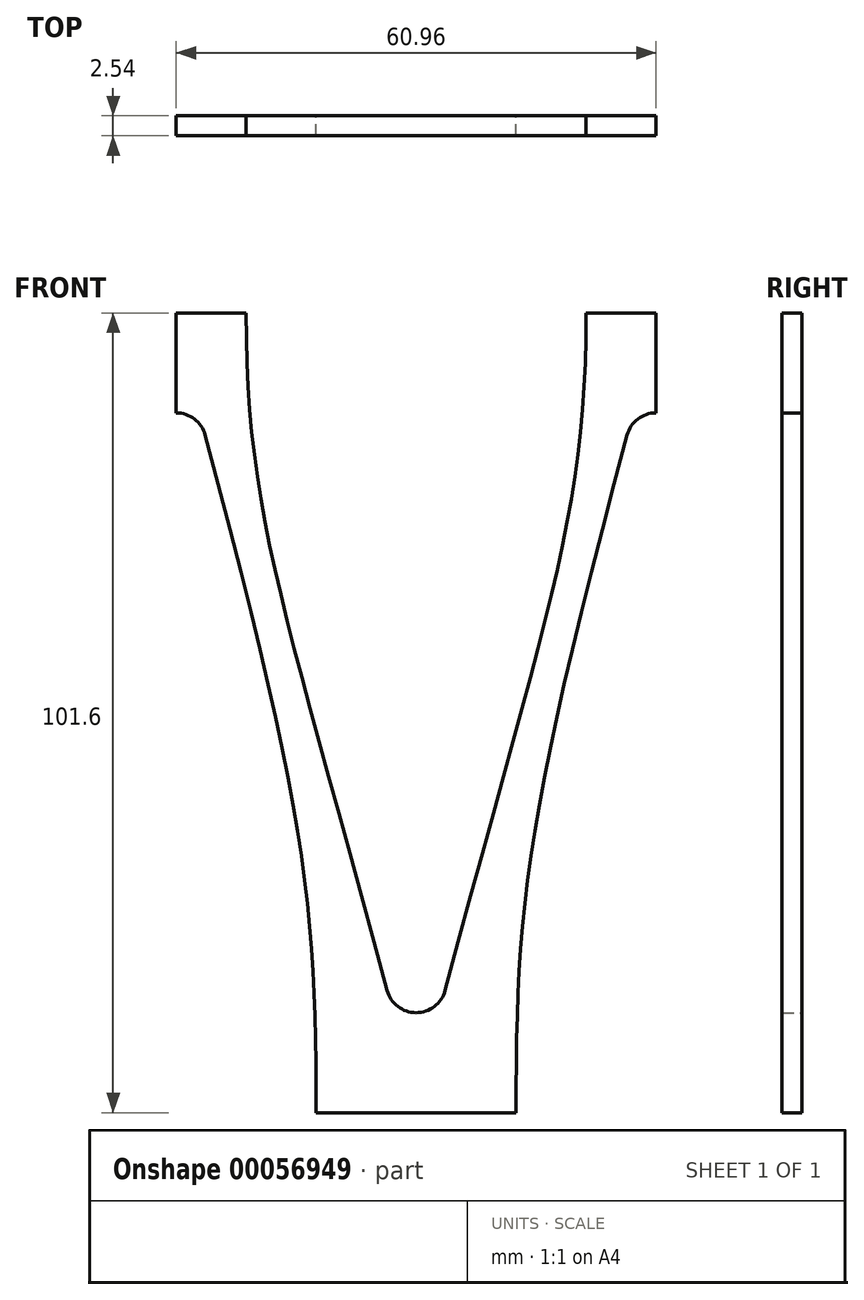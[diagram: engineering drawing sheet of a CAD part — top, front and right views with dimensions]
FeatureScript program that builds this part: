
annotation { "Feature Type Name" : "Feature", "Feature Type Description" : "" }
export const myFeature = defineFeature(function(context is Context, id is Id, definition is map)
    precondition{}
    {
        {
            var Q0;
            Q0=qCreatedBy(makeId("Front.planeOp"),FACE);
            var sketch = newSketch(context, id + "F0", { "sketchPlane" : qUnion([Q0])});
            skLineSegment(sketch, "E0", {"start": v(38.1, 139.7) * mm, "end": v(46.99, 139.7) * mm});
            skLineSegment(sketch, "E1", {"start": v(55.88, 38.1) * mm, "end": v(68.58, 38.1) * mm});
            skLineSegment(sketch, "E2", {"start": v(68.58, 38.1) * mm, "end": v(68.58, 50.8) * mm});
            skLineSegment(sketch, "E3", {"start": v(38.1, 139.7) * mm, "end": v(38.1, 127) * mm});
            skArc(sketch, "E4", {"start": v(41.78, 124.18) * mm, "mid": v(40.42, 126.21) * mm, "end": v(38.1, 127) * mm});
            skArc(sketch, "E5", {"start": v(64.9, 53.62) * mm, "mid": v(66.26, 51.59) * mm, "end": v(68.58, 50.8) * mm});
            skLineSegment(sketch, "E6", {"start": v(41.78, 124.18) * mm, "end": v(38.1, 123.2) * mm, "construction": true});
            skLineSegment(sketch, "E7", {"start": v(64.9, 53.62) * mm, "end": v(68.58, 54.61) * mm, "construction": true});
            skFitSpline(sketch, "E8", {"points": [v(55.88, 38.1) * mm, v(41.78, 124.18) * mm], "startDerivative": vector(0, 76.2) * mm, "endDerivative": vector(-39.44, 147.2) * mm});
            skFitSpline(sketch, "E9", {"points": [v(46.99, 139.7) * mm, v(64.9, 53.62) * mm], "startDerivative": vector(0, -76.2) * mm, "endDerivative": vector(39.44, -147.2) * mm});
            skPoint(sketch, "E10", {"position": v(81.28, 38.1) * mm});
            skPoint(sketch, "E11", {"position": v(98.02, 77.7) * mm});
            skPoint(sketch, "E12", {"position": v(29.21, 139.7) * mm});
            skPoint(sketch, "E13", {"position": v(38.1, 152.4) * mm});
            skPoint(sketch, "E14", {"position": v(68.58, 25.4) * mm});
            skLineSegment(sketch, "E15", {"start": v(47, 139.7) * mm, "end": v(47, 165.1) * mm, "construction": true});
            skLineSegment(sketch, "E16", {"start": v(55.88, 38.1) * mm, "end": v(55.88, 12.7) * mm, "construction": true});
            skCircle(sketch, "E17", {"center": v(55.88, 38.1) * mm, "radius": 25.4 * mm, "construction": true});
            skCircle(sketch, "E18", {"center": v(46.99, 139.7) * mm, "radius": 25.4 * mm, "construction": true});
            skSolve(sketch);
        }
        {
            var Q0;
            Q0 = qSketchRegion(id + "F0", true);
            extrude(context, id + "F1", {"entities" : qUnion([Q0]), "depth" : 2.54 * mm});
        }
        {
            var Q0;
            Q0=makeQuery(id+"F1.opExtrude","SWEPT_BODY",BODY,{"disambiguationData":[OSD([sQuery(id+"F0.wireOp",EDGE,"E0"),sQuery(id+"F0.wireOp",EDGE,"E1"),sQuery(id+"F0.wireOp",EDGE,"E2"),sQuery(id+"F0.wireOp",EDGE,"E3"),sQuery(id+"F0.wireOp",EDGE,"E4"),sQuery(id+"F0.wireOp",EDGE,"E5"),sQuery(id+"F0.wireOp",EDGE,"E8"),sQuery(id+"F0.wireOp",EDGE,"E9")])]});
            var Q1;
            Q1=makeQuery(id+"F1.opExtrude","SWEPT_FACE",FACE,{"disambiguationData":[OSD([sQuery(id+"F0.wireOp",EDGE,"E2")])]});
            mirror(context, id + "F2", {"operationType" : NewBodyOperationType.ADD, "entities" : qUnion([Q0]), "mirrorPlane" : qUnion([Q1])});
        }
    });
